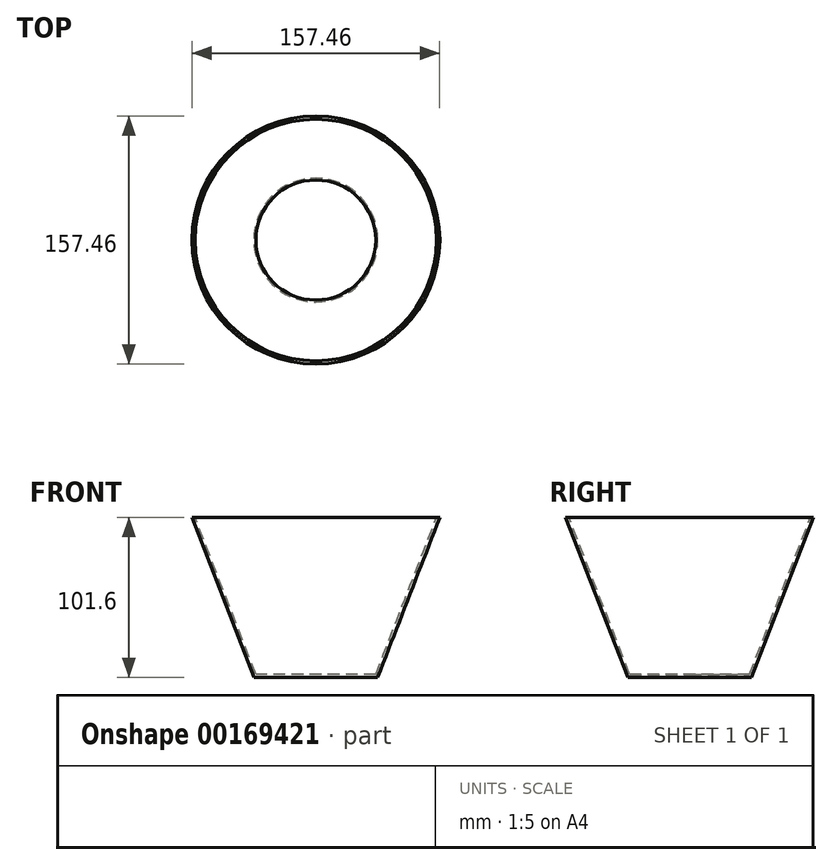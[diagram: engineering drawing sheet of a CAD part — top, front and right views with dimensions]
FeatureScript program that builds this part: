
annotation { "Feature Type Name" : "Feature", "Feature Type Description" : "" }
export const myFeature = defineFeature(function(context is Context, id is Id, definition is map)
    precondition{}
    {
        {
            var Q0;
            Q0=qCreatedBy(makeId("Front.planeOp"),FACE);
            var sketch = newSketch(context, id + "F0", { "sketchPlane" : qUnion([Q0])});
            skLineSegment(sketch, "E0", {"start": v(0, 0) * mm, "end": v(-39.32, 0) * mm});
            skLineSegment(sketch, "E1", {"start": v(-39.32, 0) * mm, "end": v(-78.73, 101.6) * mm});
            skLineSegment(sketch, "E2", {"start": v(-78.73, 101.6) * mm, "end": v(-76.73, 101.6) * mm});
            skLineSegment(sketch, "E3", {"start": v(-76.73, 101.6) * mm, "end": v(-38.1, 2) * mm});
            skLineSegment(sketch, "E4", {"start": v(-38.1, 2) * mm, "end": v(0, 2) * mm});
            skLineSegment(sketch, "E5", {"start": v(0, 2) * mm, "end": v(0, 0) * mm});
            skSolve(sketch);
        }
        {
            var Q0;
            Q0=makeQuery(id+"F0.imprint","IMPRINT",FACE,{"disambiguationData":[TD([[makeQuery(id+"F0.imprint","IMPRINT",EDGE,{"derivedFrom":sQuery(id+"F0.wireOp",EDGE,"E0")}),-1.0]])]});
            var Q1;
            Q1=sQuery(id+"F0.wireOp",EDGE,"E5");
            revolve(context, id + "F1", {"entities" : qUnion([Q0]), "axis" : qUnion([Q1]), "revolveType" : RevolveType.FULL});
        }
    });
